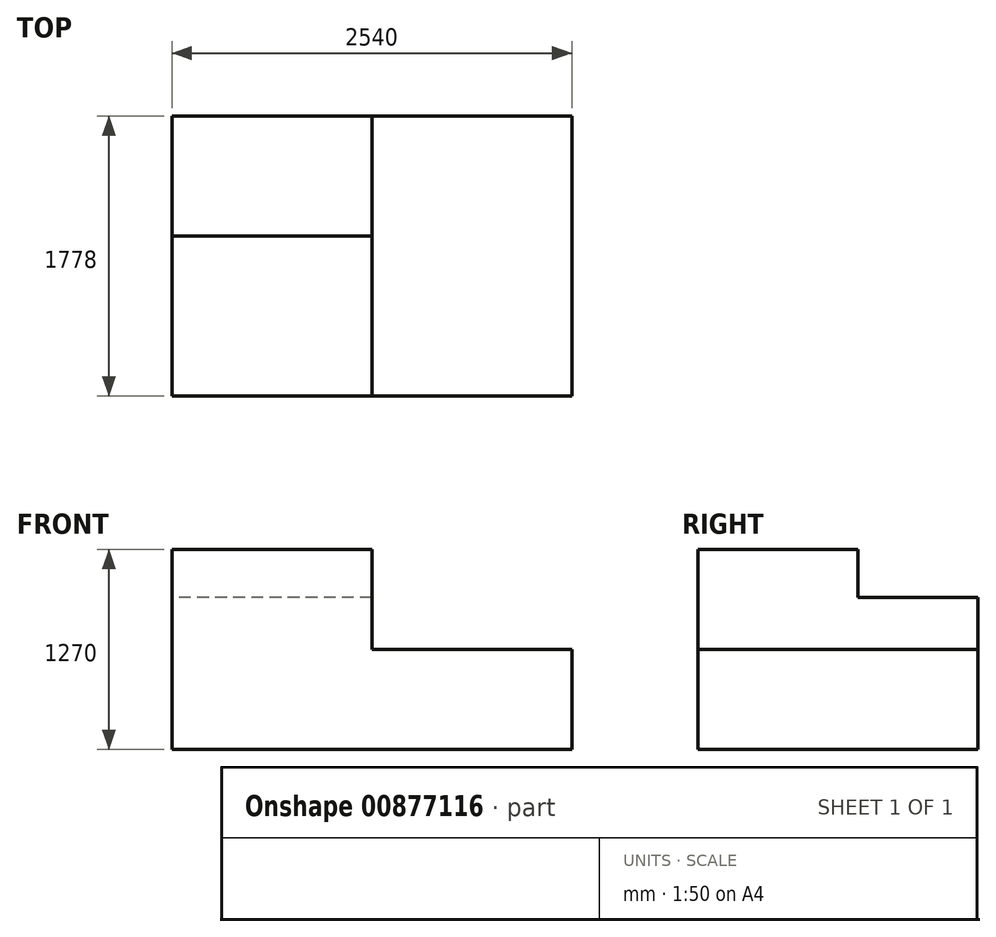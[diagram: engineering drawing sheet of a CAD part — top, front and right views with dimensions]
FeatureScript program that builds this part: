
annotation { "Feature Type Name" : "Feature", "Feature Type Description" : "" }
export const myFeature = defineFeature(function(context is Context, id is Id, definition is map)
    precondition{}
    {
        {
            var Q0;
            Q0=qCreatedBy(makeId("Top.planeOp"),FACE);
            var sketch = newSketch(context, id + "F0", { "sketchPlane" : qUnion([Q0])});
            skLineSegment(sketch, "E0.bottom", {"start": v(0, 0) * mm, "end": v(-2540, 0) * mm});
            skLineSegment(sketch, "E0.top", {"start": v(0, 1778) * mm, "end": v(-2540, 1778) * mm});
            skLineSegment(sketch, "E0.left", {"start": v(0, 0) * mm, "end": v(0, 1778) * mm});
            skLineSegment(sketch, "E0.right", {"start": v(-2540, 0) * mm, "end": v(-2540, 1778) * mm});
            skSolve(sketch);
        }
        {
            var Q0;
            Q0 = qSketchRegion(id + "F0", true);
            var Q1;
            Q1=makeQuery(id+"F0.imprint","IMPRINT",FACE,{"disambiguationData":[TD([[makeQuery(id+"F0.imprint","IMPRINT",EDGE,{"derivedFrom":sQuery(id+"F0.wireOp",EDGE,"E0.bottom")}),-1.0]])]});
            extrude(context, id + "F1", {"entities" : qUnion([Q0, Q1]), "depth" : 635 * mm, "offsetDistance" : 25.4 * mm});
        }
        {
            var Q0;
            Q0=makeQuery(id+"F1.opExtrude","CAP_FACE",FACE,{"disambiguationData":[OSD([sQuery(id+"F0.wireOp",EDGE,"E0.bottom"),sQuery(id+"F0.wireOp",EDGE,"E0.top"),sQuery(id+"F0.wireOp",EDGE,"E0.left"),sQuery(id+"F0.wireOp",EDGE,"E0.right")])],"isStart":false});
            var sketch = newSketch(context, id + "F2", { "sketchPlane" : qUnion([Q0])});
            skLineSegment(sketch, "E1.bottom", {"start": v(-2540, 0) * mm, "end": v(-1270, 0) * mm});
            skLineSegment(sketch, "E1.top", {"start": v(-2540, 1016) * mm, "end": v(-1270, 1016) * mm});
            skLineSegment(sketch, "E1.left", {"start": v(-2540, 0) * mm, "end": v(-2540, 1016) * mm});
            skLineSegment(sketch, "E1.right", {"start": v(-1270, 0) * mm, "end": v(-1270, 1016) * mm});
            skSolve(sketch);
        }
        {
            var Q0;
            Q0=makeQuery(id+"F2.imprint","IMPRINT",FACE,{"disambiguationData":[TD([[makeQuery(id+"F2.imprint","IMPRINT",EDGE,{"derivedFrom":sQuery(id+"F2.wireOp",EDGE,"E1.bottom")}),-1.0]])]});
            extrude(context, id + "F3", {"entities" : qUnion([Q0]), "operationType" : NewBodyOperationType.ADD, "depth" : 635 * mm, "offsetDistance" : 25.4 * mm});
        }
        {
            var Q0;
            Q0=makeQuery(id+"F1.opExtrude","CAP_FACE",FACE,{"disambiguationData":[OSD([sQuery(id+"F0.wireOp",EDGE,"E0.bottom"),sQuery(id+"F0.wireOp",EDGE,"E0.top"),sQuery(id+"F0.wireOp",EDGE,"E0.left"),sQuery(id+"F0.wireOp",EDGE,"E0.right")])],"isStart":false});
            var sketch = newSketch(context, id + "F4", { "sketchPlane" : qUnion([Q0])});
            skLineSegment(sketch, "E2.bottom", {"start": v(-2540, 1016) * mm, "end": v(-1270, 1016) * mm});
            skLineSegment(sketch, "E2.top", {"start": v(-2540, 1778) * mm, "end": v(-1270, 1778) * mm});
            skLineSegment(sketch, "E2.left", {"start": v(-2540, 1016) * mm, "end": v(-2540, 1778) * mm});
            skLineSegment(sketch, "E2.right", {"start": v(-1270, 1016) * mm, "end": v(-1270, 1778) * mm});
            skSolve(sketch);
        }
        {
            var Q0;
            Q0=makeQuery(id+"F4.imprint","IMPRINT",FACE,{"disambiguationData":[TD([[makeQuery(id+"F4.imprint","IMPRINT",EDGE,{"derivedFrom":sQuery(id+"F4.wireOp",EDGE,"E2.bottom")}),1.0]])]});
            extrude(context, id + "F5", {"entities" : qUnion([Q0]), "operationType" : NewBodyOperationType.ADD, "depth" : 330.2 * mm, "offsetDistance" : 25.4 * mm});
        }
    });
